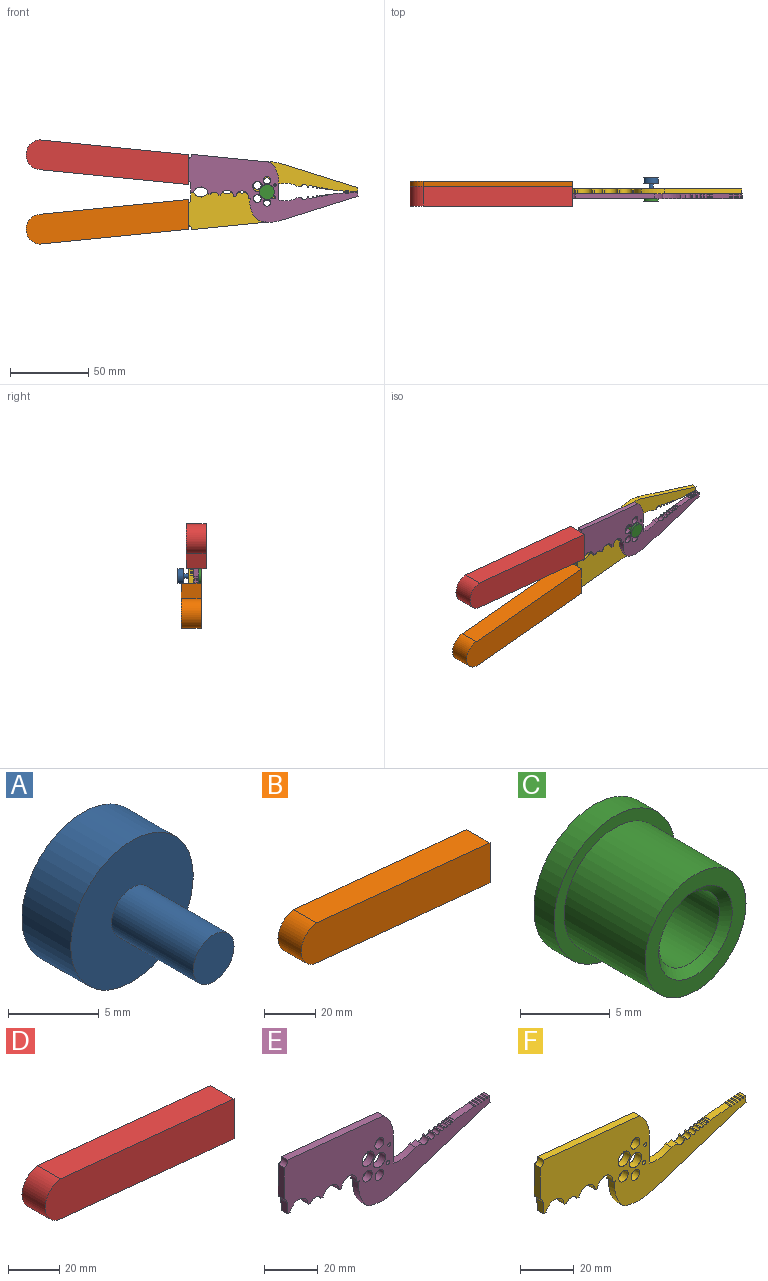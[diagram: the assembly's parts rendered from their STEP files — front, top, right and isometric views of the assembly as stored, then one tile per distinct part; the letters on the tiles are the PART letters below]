
ASSEMBLY  parts=6 mates=5
PART A: 5 faces, bbox 9.5x10.2x9.5 mm
  f0: cylinder r=4.76mm len=9.53mm, axis (0,1,0), area 114mm2, adj f1,f2
  f1: plane 9.53x9.53mm, normal (0,-1,0), area 63.3mm2, adj f0,f3
  f2: plane 9.53x9.53mm, normal (0,1,0), area 71.3mm2, adj f0
  f3: cylinder r=1.59mm len=6.35mm, axis (0,1,0), area 63.3mm2, adj f1,f4
  f4: plane 3.18x3.18mm, normal (0,-1,0), area 7.9mm2, adj f3
PART B: 6 faces, bbox 103.9x12.7x28.6 mm
  f0: plane 19.05x12.7mm, normal (1,0,0), area 241.9mm2, adj f1,f3,f4,f5
  f1: plane 95.25x12.7mm, normal (0.1,0,1), area 1215.7mm2, adj f0,f2,f4,f5
  f2: cylinder r=9.57mm len=19.05mm, axis (0,1,0), area 357.7mm2, adj f1,f3,f4,f5
  f3: plane 95.25x12.7mm, normal (-0.1,0,-1), area 1215.7mm2, adj f0,f2,f4,f5
  f4: plane 103.87x28.58mm, normal (0,-1,0), area 1940.2mm2, adj f0,f1,f2,f3
  f5: plane 103.87x28.58mm, normal (0,1,0), area 1940.2mm2, adj f0,f1,f2,f3
PART C: 8 faces, bbox 9.5x7.9x9.5 mm
  f0: cylinder r=4.76mm len=9.53mm, axis (0,1,0), area 47.5mm2, adj f1,f2
  f1: plane 9.53x9.53mm, normal (0,-1,0), area 21.8mm2, adj f0,f4
  f2: plane 9.53x9.53mm, normal (0,1,0), area 71.3mm2, adj f0
  f3: cylinder r=2.38mm len=5.84mm, axis (0,1,0), area 87.4mm2, adj f6,f7
  f4: cylinder r=3.97mm len=7.94mm, axis (0,1,0), area 158.3mm2, adj f1,f5
  f5: plane 7.94x7.94mm, normal (0,-1,0), area 23.3mm2, adj f4,f7
  f6: plane 4.76x4.76mm, normal (0,-1,0), area 17.8mm2, adj f3
  f7: cone r=2.38mm half-angle=45deg, axis (0,-1,0), area 11.9mm2, adj f3,f5
PART D: 6 faces, bbox 103.9x12.7x28.6 mm
  f0: plane 19.05x12.7mm, normal (1,0,0), area 241.9mm2, adj f1,f3,f4,f5
  f1: plane 95.25x12.7mm, normal (0.1,0,1), area 1215.7mm2, adj f0,f2,f4,f5
  f2: cylinder r=9.57mm len=19.05mm, axis (0,1,0), area 357.7mm2, adj f1,f3,f4,f5
  f3: plane 95.25x12.7mm, normal (-0.1,0,-1), area 1215.7mm2, adj f0,f2,f4,f5
  f4: plane 103.87x28.58mm, normal (0,-1,0), area 1940.2mm2, adj f0,f1,f2,f3
  f5: plane 103.87x28.58mm, normal (0,1,0), area 1940.2mm2, adj f0,f1,f2,f3
PART E: 57 faces, bbox 108.4x3.2x43.4 mm
  f0: cylinder r=2.03mm len=3.18mm, axis (0,1,0), area 11.6mm2, adj f1,f54,f55,f56
  f1: plane 14.47x3.18mm, normal (-1,0,0), area 45.9mm2, adj f0,f2,f55,f56
  f2: cylinder r=2.36mm len=3.18mm, axis (0,1,0), area 9.1mm2, adj f1,f3,f55,f56
  f3: plane 5.08x3.18mm, normal (-1,0,-0.01), area 16.1mm2, adj f2,f4,f55,f56
  f4: plane 3.18x1.58mm, normal (-0.1,0,-1), area 5mm2, adj f3,f5,f55,f56
  f5: cylinder r=4.83mm len=9.48mm, axis (0,1,0), area 43.2mm2, adj f4,f6,f55,f56
  f6: plane 3.18x1.15mm, normal (-0.1,0,-1), area 3.7mm2, adj f5,f7,f55,f56
  f7: cylinder r=3.4mm len=5.61mm, axis (0,1,0), area 21.1mm2, adj f6,f8,f55,f56
  f8: plane 3.18x1.14mm, normal (-0.1,0,-1), area 3.6mm2, adj f7,f9,f55,f56
  f9: cylinder r=4.28mm len=8.42mm, axis (0,1,0), area 38.6mm2, adj f8,f10,f55,f56
  f10: plane 3.18x1.29mm, normal (-0.1,0,-1), area 4.1mm2, adj f9,f11,f55,f56
  f11: cylinder r=3.96mm len=7.92mm, axis (0,1,0), area 40.8mm2, adj f10,f12,f55,f56
  f12: plane 3.18x1.38mm, normal (-0.1,0,-1), area 4.4mm2, adj f11,f13,f55,f56
  f13: cylinder r=15.41mm len=13.84mm, axis (0,1,0), area 48.1mm2, adj f12,f14,f55,f56
  f14: cylinder r=22.7mm len=14.9mm, axis (0,1,0), area 48.2mm2, adj f13,f15,f55,f56
  f15: plane 49.43x15.49mm, normal (0.3,0,-0.95), area 164.5mm2, adj f14,f16,f55,f56
  f16: plane 3.18x3.16mm, normal (0.99,0,0.11), area 10.1mm2, adj f15,f17,f55,f56
  f17: plane 3.18x0.82mm, normal (-0.11,0,0.99), area 2.6mm2, adj f16,f18,f55,f56
  f18: cylinder r=0.4mm len=3.18mm, axis (0,1,0), area 4.6mm2, adj f17,f19,f55,f56
  f19: plane 3.18x0.79mm, normal (-0.11,0,0.99), area 2.5mm2, adj f18,f20,f55,f56
  f20: cylinder r=0.42mm len=3.18mm, axis (0,1,0), area 4.9mm2, adj f19,f21,f55,f56
  f21: plane 3.18x0.79mm, normal (-0.11,0,0.99), area 2.5mm2, adj f20,f22,f55,f56
  f22: cylinder r=0.4mm len=3.18mm, axis (0,1,0), area 4.6mm2, adj f21,f23,f55,f56
  f23: plane 3.18x0.78mm, normal (-0.11,0,0.99), area 2.5mm2, adj f22,f24,f55,f56
  f24: cylinder r=0.41mm len=3.18mm, axis (0,1,0), area 4.7mm2, adj f23,f25,f55,f56
  f25: plane 3.18x0.79mm, normal (-0.11,0,0.99), area 2.5mm2, adj f24,f26,f55,f56
  f26: cylinder r=0.41mm len=3.18mm, axis (0,1,0), area 4.8mm2, adj f25,f27,f55,f56
  f27: plane 10.41x3.18mm, normal (-0.11,0,0.99), area 33.2mm2, adj f26,f28,f55,f56
  f28: cylinder r=0.14mm len=3.18mm, axis (0,1,0), area 1.8mm2, adj f27,f29,f55,f56
  f29: plane 3.18x0.63mm, normal (-0.11,0,0.99), area 2mm2, adj f28,f30,f55,f56
  f30: cylinder r=0.26mm len=3.18mm, axis (0,1,0), area 2.9mm2, adj f29,f31,f55,f56
  f31: plane 3.18x0.63mm, normal (-0.11,0,0.99), area 2mm2, adj f30,f32,f55,f56
  f32: cylinder r=0.51mm len=3.18mm, axis (0,1,0), area 4.8mm2, adj f31,f33,f55,f56
  f33: plane 3.18x0.64mm, normal (-0.11,0,0.99), area 2.1mm2, adj f32,f34,f55,f56
  f34: cylinder r=0.7mm len=3.18mm, axis (0,1,0), area 6.8mm2, adj f33,f35,f55,f56
  f35: plane 3.18x0.63mm, normal (-0.11,0,0.99), area 2mm2, adj f34,f36,f55,f56
  f36: cylinder r=0.83mm len=3.18mm, axis (0,1,0), area 8.3mm2, adj f35,f37,f55,f56
  f37: plane 3.18x0.63mm, normal (-0.11,0,0.99), area 2mm2, adj f36,f38,f55,f56
  f38: cylinder r=0.96mm len=3.18mm, axis (0,1,0), area 10.5mm2, adj f37,f39,f55,f56
  f39: plane 3.18x0.64mm, normal (-0.11,0,0.99), area 2mm2, adj f38,f40,f55,f56
  f40: cylinder r=1.28mm len=3.18mm, axis (0,1,0), area 13.5mm2, adj f39,f41,f55,f56
  f41: plane 3.18x0.63mm, normal (-0.11,0,0.99), area 2mm2, adj f40,f42,f55,f56
  f42: cylinder r=1.95mm len=3.79mm, axis (0,1,0), area 16.8mm2, adj f41,f43,f55,f56
  f43: plane 3.18x2.94mm, normal (-0.11,0,0.99), area 9.4mm2, adj f42,f44,f55,f56
  f44: cylinder r=15.25mm len=11.83mm, axis (0,1,0), area 38.8mm2, adj f43,f45,f55,f56
  f45: plane 10.8x3.18mm, normal (1,0,0), area 34.3mm2, adj f44,f46,f55,f56
  f46: cylinder r=15.88mm len=13.27mm, axis (0,1,0), area 46.7mm2, adj f45,f54,f55,f56
  f47: cylinder r=3.17mm len=6.35mm, axis (0,1,0), area 63.3mm2, adj f55,f56
  f48: cylinder r=2.38mm len=4.76mm, axis (0,1,0), area 47.5mm2, adj f55,f56
  f49: cylinder r=0.79mm len=3.18mm, axis (0,1,0), area 15.8mm2, adj f55,f56
  f50: cylinder r=0.91mm len=3.18mm, axis (0,1,0), area 18.2mm2, adj f55,f56
  f51: cylinder r=2.31mm len=4.62mm, axis (0,1,0), area 46.1mm2, adj f55,f56
  f52: cylinder r=2.45mm len=4.91mm, axis (0,1,0), area 49mm2, adj f55,f56
  f53: cylinder r=3.17mm len=6.35mm, axis (0,1,0), area 63.3mm2, adj f55,f56
  f54: plane 50.55x5.05mm, normal (0.1,0,1), area 161.3mm2, adj f0,f46,f55,f56
  f55: plane 108.36x43.41mm, normal (0,-1,0), area 1802mm2, adj f0,f1,f2,f3,f4,f5,f6,f7
  f56: plane 108.36x43.41mm, normal (0,1,0), area 1802mm2, adj f0,f1,f2,f3,f4,f5,f6,f7
PART F: 57 faces, bbox 108.4x3.2x43.4 mm
  f0: cylinder r=2.03mm len=3.18mm, axis (0,1,0), area 11.6mm2, adj f1,f54,f55,f56
  f1: plane 14.47x3.18mm, normal (-1,0,0), area 45.9mm2, adj f0,f2,f55,f56
  f2: cylinder r=2.36mm len=3.18mm, axis (0,1,0), area 9.1mm2, adj f1,f3,f55,f56
  f3: plane 5.08x3.18mm, normal (-1,0,-0.01), area 16.1mm2, adj f2,f4,f55,f56
  f4: plane 3.18x1.58mm, normal (-0.1,0,-1), area 5mm2, adj f3,f5,f55,f56
  f5: cylinder r=4.83mm len=9.48mm, axis (0,1,0), area 43.2mm2, adj f4,f6,f55,f56
  f6: plane 3.18x1.15mm, normal (-0.1,0,-1), area 3.7mm2, adj f5,f7,f55,f56
  f7: cylinder r=3.4mm len=5.61mm, axis (0,1,0), area 21.1mm2, adj f6,f8,f55,f56
  f8: plane 3.18x1.14mm, normal (-0.1,0,-1), area 3.6mm2, adj f7,f9,f55,f56
  f9: cylinder r=4.28mm len=8.42mm, axis (0,1,0), area 38.6mm2, adj f8,f10,f55,f56
  f10: plane 3.18x1.29mm, normal (-0.1,0,-1), area 4.1mm2, adj f9,f11,f55,f56
  f11: cylinder r=3.96mm len=7.92mm, axis (0,1,0), area 40.8mm2, adj f10,f12,f55,f56
  f12: plane 3.18x1.38mm, normal (-0.1,0,-1), area 4.4mm2, adj f11,f13,f55,f56
  f13: cylinder r=15.41mm len=13.84mm, axis (0,1,0), area 48.1mm2, adj f12,f14,f55,f56
  f14: cylinder r=22.7mm len=14.9mm, axis (0,1,0), area 48.2mm2, adj f13,f15,f55,f56
  f15: plane 49.43x15.49mm, normal (0.3,0,-0.95), area 164.5mm2, adj f14,f16,f55,f56
  f16: plane 3.18x3.16mm, normal (0.99,0,0.11), area 10.1mm2, adj f15,f17,f55,f56
  f17: plane 3.18x0.82mm, normal (-0.11,0,0.99), area 2.6mm2, adj f16,f18,f55,f56
  f18: cylinder r=0.4mm len=3.18mm, axis (0,1,0), area 4.6mm2, adj f17,f19,f55,f56
  f19: plane 3.18x0.79mm, normal (-0.11,0,0.99), area 2.5mm2, adj f18,f20,f55,f56
  f20: cylinder r=0.42mm len=3.18mm, axis (0,1,0), area 4.9mm2, adj f19,f21,f55,f56
  f21: plane 3.18x0.79mm, normal (-0.11,0,0.99), area 2.5mm2, adj f20,f22,f55,f56
  f22: cylinder r=0.4mm len=3.18mm, axis (0,1,0), area 4.6mm2, adj f21,f23,f55,f56
  f23: plane 3.18x0.78mm, normal (-0.11,0,0.99), area 2.5mm2, adj f22,f24,f55,f56
  f24: cylinder r=0.41mm len=3.18mm, axis (0,1,0), area 4.7mm2, adj f23,f25,f55,f56
  f25: plane 3.18x0.79mm, normal (-0.11,0,0.99), area 2.5mm2, adj f24,f26,f55,f56
  f26: cylinder r=0.41mm len=3.18mm, axis (0,1,0), area 4.8mm2, adj f25,f27,f55,f56
  f27: plane 10.41x3.18mm, normal (-0.11,0,0.99), area 33.2mm2, adj f26,f28,f55,f56
  f28: cylinder r=0.14mm len=3.18mm, axis (0,1,0), area 1.8mm2, adj f27,f29,f55,f56
  f29: plane 3.18x0.63mm, normal (-0.11,0,0.99), area 2mm2, adj f28,f30,f55,f56
  f30: cylinder r=0.26mm len=3.18mm, axis (0,1,0), area 2.9mm2, adj f29,f31,f55,f56
  f31: plane 3.18x0.63mm, normal (-0.11,0,0.99), area 2mm2, adj f30,f32,f55,f56
  f32: cylinder r=0.51mm len=3.18mm, axis (0,1,0), area 4.8mm2, adj f31,f33,f55,f56
  f33: plane 3.18x0.64mm, normal (-0.11,0,0.99), area 2.1mm2, adj f32,f34,f55,f56
  f34: cylinder r=0.7mm len=3.18mm, axis (0,1,0), area 6.8mm2, adj f33,f35,f55,f56
  f35: plane 3.18x0.63mm, normal (-0.11,0,0.99), area 2mm2, adj f34,f36,f55,f56
  f36: cylinder r=0.83mm len=3.18mm, axis (0,1,0), area 8.3mm2, adj f35,f37,f55,f56
  f37: plane 3.18x0.63mm, normal (-0.11,0,0.99), area 2mm2, adj f36,f38,f55,f56
  f38: cylinder r=0.96mm len=3.18mm, axis (0,1,0), area 10.5mm2, adj f37,f39,f55,f56
  f39: plane 3.18x0.64mm, normal (-0.11,0,0.99), area 2mm2, adj f38,f40,f55,f56
  f40: cylinder r=1.28mm len=3.18mm, axis (0,1,0), area 13.5mm2, adj f39,f41,f55,f56
  f41: plane 3.18x0.63mm, normal (-0.11,0,0.99), area 2mm2, adj f40,f42,f55,f56
  f42: cylinder r=1.95mm len=3.79mm, axis (0,1,0), area 16.8mm2, adj f41,f43,f55,f56
  f43: plane 3.18x2.94mm, normal (-0.11,0,0.99), area 9.4mm2, adj f42,f44,f55,f56
  f44: cylinder r=15.25mm len=11.83mm, axis (0,1,0), area 38.8mm2, adj f43,f45,f55,f56
  f45: plane 10.8x3.18mm, normal (1,0,0), area 34.3mm2, adj f44,f46,f55,f56
  f46: cylinder r=15.88mm len=13.27mm, axis (0,1,0), area 46.7mm2, adj f45,f54,f55,f56
  f47: cylinder r=3.17mm len=6.35mm, axis (0,1,0), area 63.3mm2, adj f55,f56
  f48: cylinder r=2.38mm len=4.76mm, axis (0,1,0), area 47.5mm2, adj f55,f56
  f49: cylinder r=0.79mm len=3.18mm, axis (0,1,0), area 15.8mm2, adj f55,f56
  f50: cylinder r=0.91mm len=3.18mm, axis (0,1,0), area 18.2mm2, adj f55,f56
  f51: cylinder r=2.31mm len=4.62mm, axis (0,1,0), area 46.1mm2, adj f55,f56
  f52: cylinder r=2.45mm len=4.91mm, axis (0,1,0), area 49mm2, adj f55,f56
  f53: cylinder r=3.17mm len=6.35mm, axis (0,1,0), area 63.3mm2, adj f55,f56
  f54: plane 50.55x5.05mm, normal (0.1,0,1), area 161.3mm2, adj f0,f46,f55,f56
  f55: plane 108.36x43.41mm, normal (0,-1,0), area 1802mm2, adj f0,f1,f2,f3,f4,f5,f6,f7
  f56: plane 108.36x43.41mm, normal (0,1,0), area 1802mm2, adj f0,f1,f2,f3,f4,f5,f6,f7
PLACE A t=(259.71,45.03,-35.33)mm
PLACE B rot(axis=(1,0,0),180deg) t=(103.05,36.46,-82.5)mm fixed
PLACE C rot(axis=(1,0,0),180deg) t=(244.98,30.11,-8.19)mm
PLACE D t=(-3.35,33.28,-17.25)mm
PLACE E t=(-3.35,33.28,-17.01)mm
PLACE F rot(axis=(1,0,0),180deg) t=(103.05,36.46,-82.75)mm
MATE fastened B.f0 <-> F.f1  axis (1,0,0) through (10.18,36.46,-22.49)mm
MATE fastened D.f0 <-> E.f1  axis (1,0,0) through (10.18,33.28,6.11)mm
MATE revolute A.f0 <-> E.f53  axis (0,-1,0) through (60.36,34.87,-8.19)mm
MATE revolute F.f53 <-> E.f53  axis (0,-1,0) through (60.36,34.87,-8.19)mm
MATE revolute C.f0 <-> E.f53  axis (0,1,0) through (60.36,31.7,-8.19)mm
